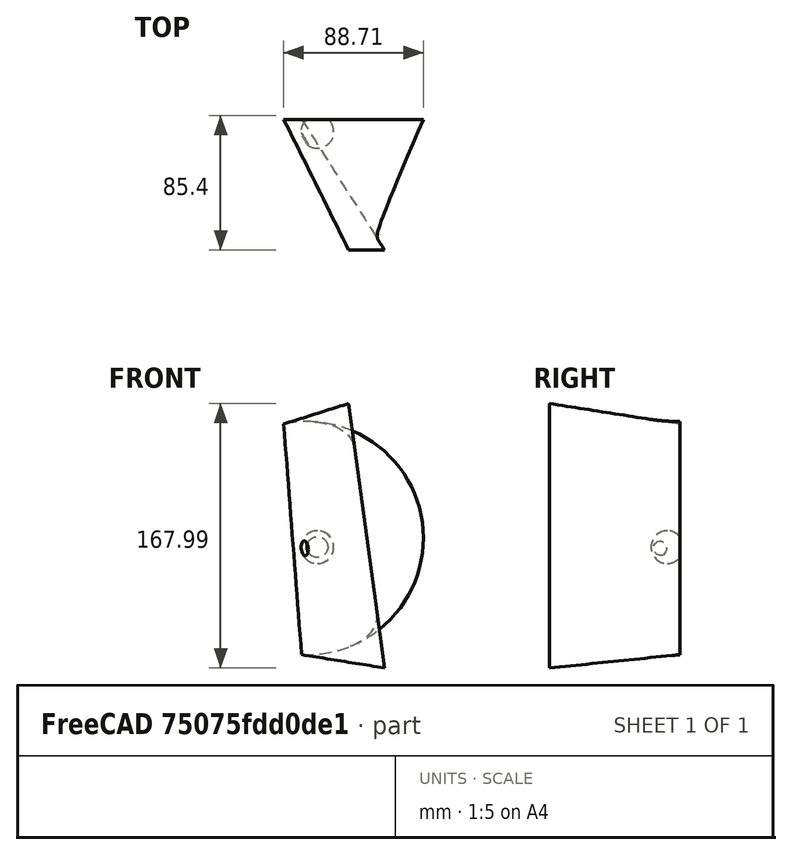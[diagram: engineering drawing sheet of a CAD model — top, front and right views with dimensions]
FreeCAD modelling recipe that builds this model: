
FCSTD DOCUMENT  (FreeCAD 0.20R29410 (Git))
Label: MangoJelly_Solutions_Tutorial_Ep10_1
License: All rights reserved
LicenseURL: http://en.wikipedia.org/wiki/All_rights_reserved
objects: Part::RuledSurface×3, Sketcher::SketchObject×2, Part::Compound×1, Part::Feature×1, Part::Sphere×1, Part::Cut×1
note: 9 computed .brp shape members not serialized (recipe doc carries the construction recipe); baked Part::Feature solids carry a one-line shape summary decoded from their .brp

FEATURE [Sketcher::SketchObject] Sketch
  FullyConstrained = false
  Placement = pos=(0,20,0) rot=(1,0,0;1.5708rad)
  sketch-geometry (1):
    g0: ArcOfCircle CenterX=32.2763 CenterY=5.69137 CenterZ=0 NormalX=0 NormalY=0 NormalZ=1 AngleXU=0 Radius=74.0279 StartAngle=4.66761 EndAngle=8.05363
FEATURE [Sketcher::SketchObject] Sketch001
  FullyConstrained = false
  Placement = pos=(0,-63,0) rot=(1,0,0;1.5708rad)
  sketch-geometry (1):
    g0: LineSegment StartX=58.8981 StartY=91.2562 StartZ=0 EndX=81.6326 EndY=-76.7265 EndZ=0
FEATURE [Part::RuledSurface] Ruled_Surface
  Curve1 = -> Sketch [Edge1]
  Curve2 = -> Sketch001 [Edge1]
  Orientation = 0
FEATURE [Part::RuledSurface] Ruled_Surface001
  Curve1 = -> Ruled_Surface [Edge2]
  Curve2 = -> Ruled_Surface [Edge4]
  Orientation = 0
FEATURE [Part::RuledSurface] Ruled_Surface002
  Curve1 = -> Sketch [Edge1]
  Curve2 = -> Ruled_Surface001 [Edge4]
  Orientation = 0
FEATURE [Part::Compound] Compound
  Links = -> [Ruled_Surface,Ruled_Surface002,Ruled_Surface001]
FEATURE [Part::Feature] Compound_solid  label="Compound (Solid)"
  shape: bbox 99.96 x 83 x 168 mm, 3 faces (baked)
FEATURE [Part::Sphere] Sphere
  Angle1 = -90
  Angle2 = 90
  Angle3 = 360
  AttacherType = Attacher::AttachEngine3D
  Placement = pos=(39,12,0) rot=(0,0,1;0rad)
  Radius = 10.4
FEATURE [Part::Cut] Cut
  Base = -> Compound_solid
  Tool = -> Sphere
